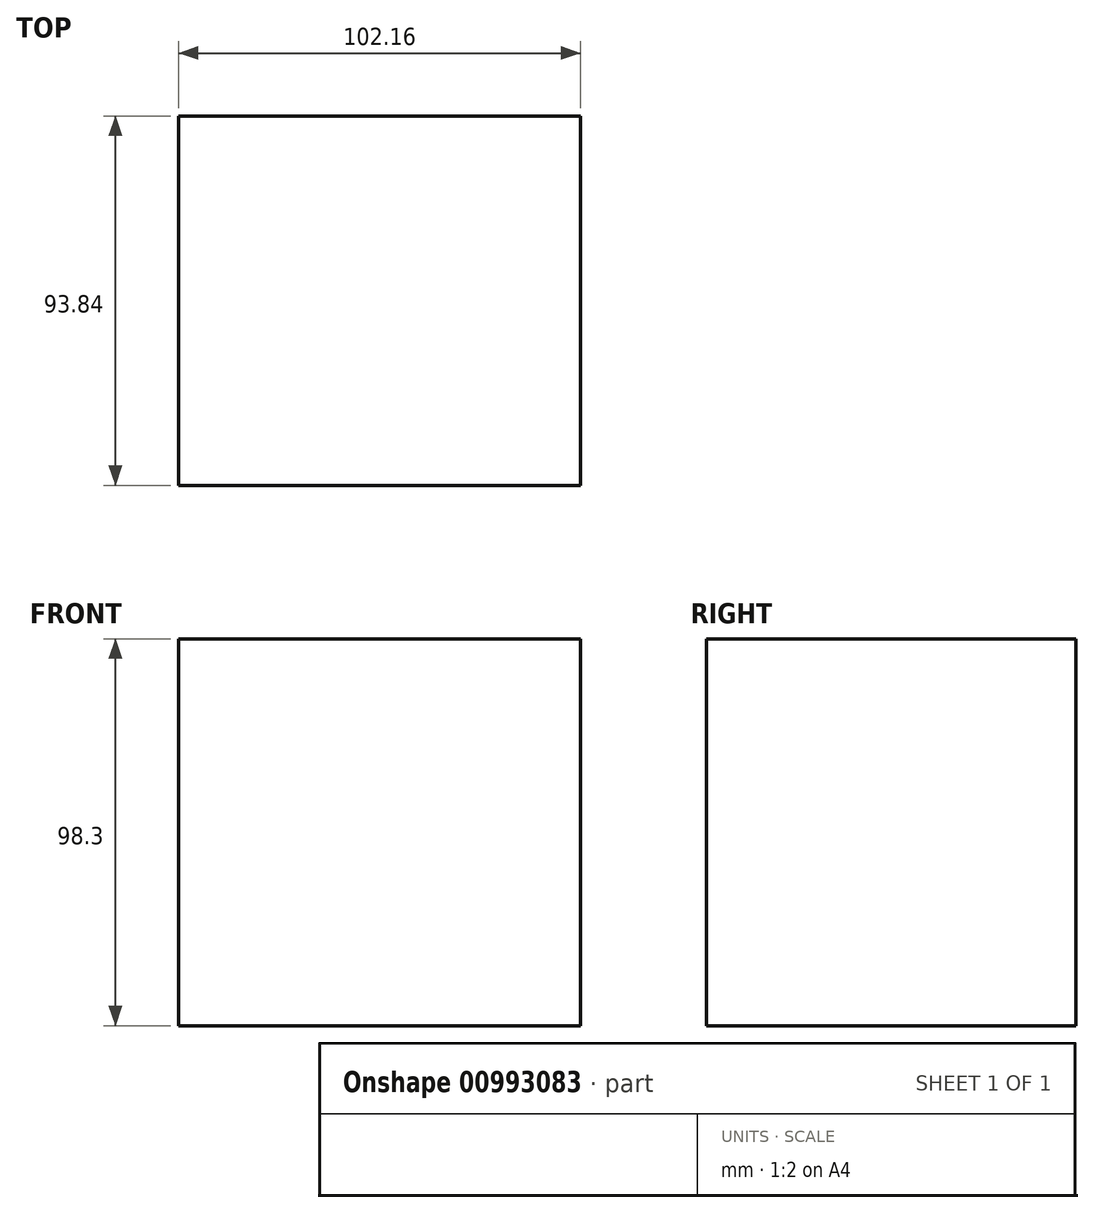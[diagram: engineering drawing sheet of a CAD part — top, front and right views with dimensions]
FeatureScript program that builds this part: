
annotation { "Feature Type Name" : "Feature", "Feature Type Description" : "" }
export const myFeature = defineFeature(function(context is Context, id is Id, definition is map)
    precondition{}
    {
        {
            var Q0;
            Q0=qCreatedBy(makeId("Top.planeOp"),FACE);
            var sketch = newSketch(context, id + "F0", { "sketchPlane" : qUnion([Q0])});
            skLineSegment(sketch, "E0.bottom", {"start": v(55.13, 46.92) * mm, "end": v(-47.03, 46.92) * mm});
            skLineSegment(sketch, "E0.top", {"start": v(55.13, -46.92) * mm, "end": v(-47.03, -46.92) * mm});
            skLineSegment(sketch, "E0.left", {"start": v(55.13, 46.92) * mm, "end": v(55.13, -46.92) * mm});
            skLineSegment(sketch, "E0.right", {"start": v(-47.03, 46.92) * mm, "end": v(-47.03, -46.92) * mm});
            skPoint(sketch, "E0.middle", {"position": v(4.05, 0) * mm});
            skSolve(sketch);
        }
        {
            var Q0;
            Q0=makeQuery(id+"F0.imprint","IMPRINT",FACE,{"disambiguationData":[TD([[makeQuery(id+"F0.imprint","IMPRINT",EDGE,{"derivedFrom":sQuery(id+"F0.wireOp",EDGE,"E0.bottom")}),1.0]])]});
            extrude(context, id + "F1", {"entities" : qUnion([Q0]), "depth" : 98.3 * mm, "offsetDistance" : 25.4 * mm});
        }
    });
